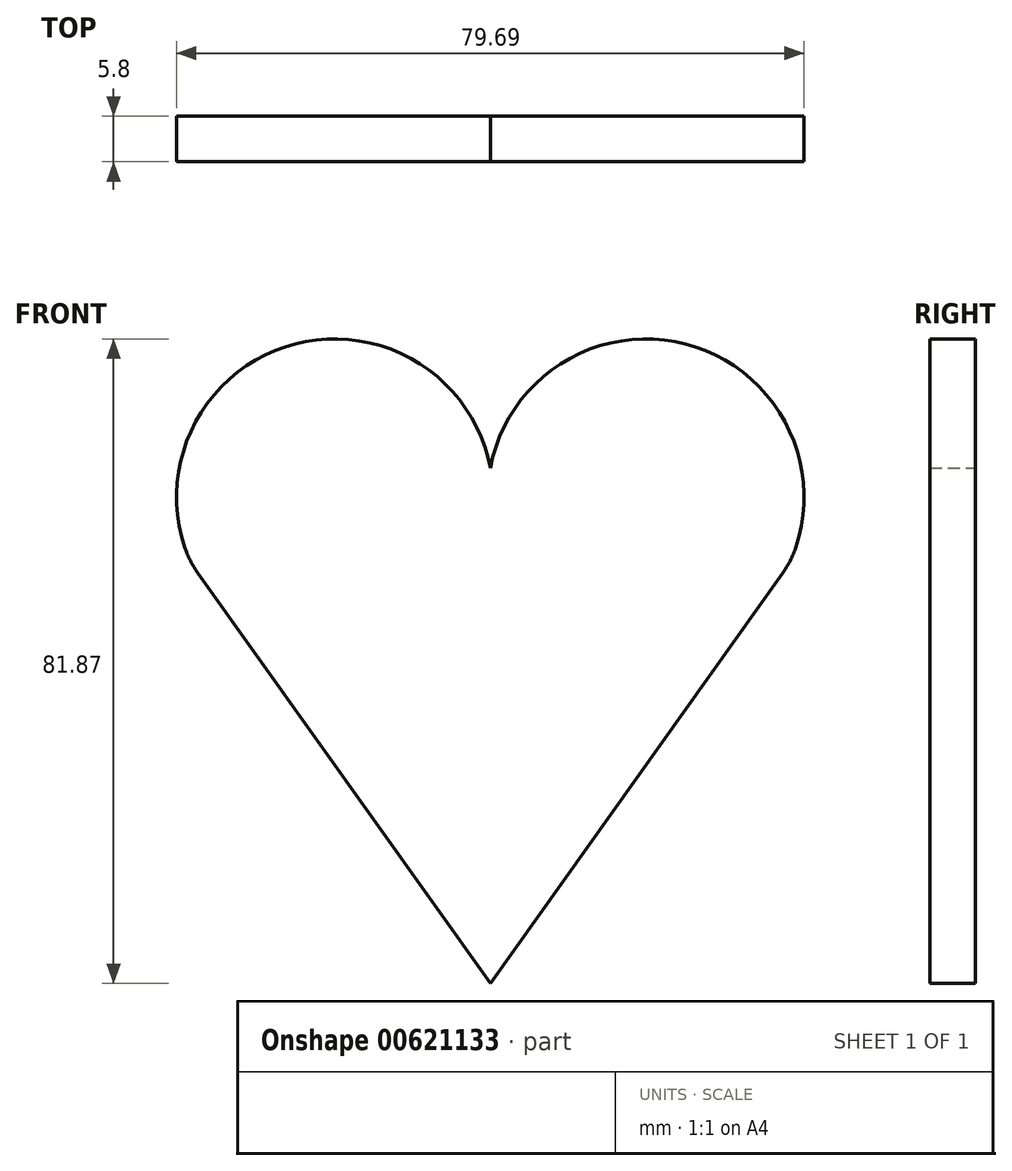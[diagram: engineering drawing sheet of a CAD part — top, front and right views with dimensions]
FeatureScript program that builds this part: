
annotation { "Feature Type Name" : "Feature", "Feature Type Description" : "" }
export const myFeature = defineFeature(function(context is Context, id is Id, definition is map)
    precondition{}
    {
        {
            var Q0;
            Q0=qCreatedBy(makeId("Front.planeOp"),FACE);
            var sketch = newSketch(context, id + "F0", { "sketchPlane" : qUnion([Q0])});
            skLineSegment(sketch, "E0", {"start": v(-43.6, 19.44) * mm, "end": v(-6.48, -32.63) * mm});
            skArc(sketch, "E1", {"start": v(-6.48, 32.83) * mm, "mid": v(-31.26, 48.6) * mm, "end": v(-45.31, 22.82) * mm});
            skPoint(sketch, "E2.visualSharp", {"position": v(-44.43, 20.61) * mm});
            skArc(sketch, "E2.filletArc", {"start": v(-45.31, 22.82) * mm, "mid": v(-44.58, 21.06) * mm, "end": v(-43.6, 19.44) * mm});
            skArc(sketch, "E3.MirrorCS", {"start": v(-68.37, -11.27) * mm, "mid": v(-75.19, 17.3) * mm, "end": v(-46.23, 22.16) * mm});
            skLineSegment(sketch, "E4", {"start": v(-68.37, -11.27) * mm, "end": v(-6.48, -32.63) * mm});
            skLineSegment(sketch, "E5", {"start": v(-6.48, 32.83) * mm, "end": v(-6.48, -32.63) * mm});
            skArc(sketch, "E6.MirrorCS", {"start": v(-6.48, 32.83) * mm, "mid": v(18.29, 48.6) * mm, "end": v(32.34, 22.82) * mm});
            skArc(sketch, "E7.MirrorCS", {"start": v(32.34, 22.82) * mm, "mid": v(31.61, 21.06) * mm, "end": v(30.63, 19.44) * mm});
            skLineSegment(sketch, "E8.MirrorCS", {"start": v(30.63, 19.44) * mm, "end": v(-6.48, -32.63) * mm});
            skSolve(sketch);
        }
        {
            var Q0;
            Q0 = qSketchRegion(id + "F0", true);
            extrude(context, id + "F1", {"entities" : qUnion([Q0]), "depth" : 5.8 * mm, "offsetDistance" : 25.4 * mm});
        }
    });
